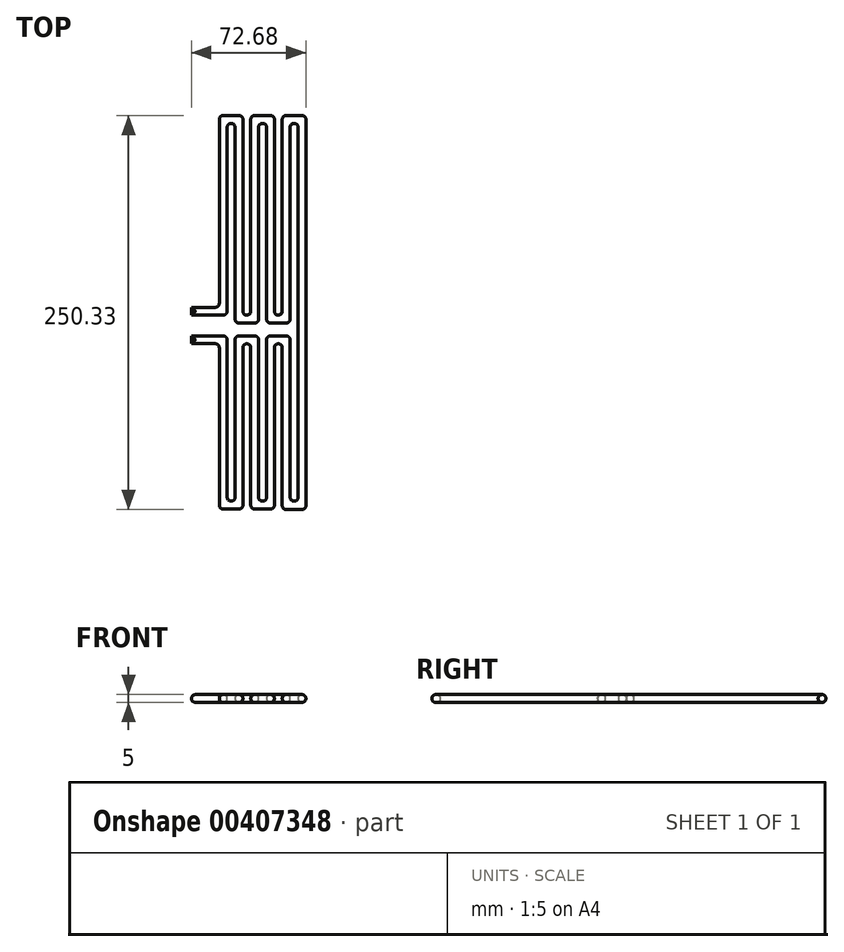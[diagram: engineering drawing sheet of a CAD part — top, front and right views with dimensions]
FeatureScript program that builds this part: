
annotation { "Feature Type Name" : "Feature", "Feature Type Description" : "" }
export const myFeature = defineFeature(function(context is Context, id is Id, definition is map)
    precondition{}
    {
        {
            var Q0;
            Q0=qCreatedBy(makeId("Top.planeOp"),FACE);
            var sketch = newSketch(context, id + "F0", { "sketchPlane" : qUnion([Q0])});
            skLineSegment(sketch, "E0.bottom", {"start": v(0, 0) * mm, "end": v(17.68, 0) * mm});
            skLineSegment(sketch, "E0.top", {"start": v(0, 5) * mm, "end": v(15.18, 5) * mm});
            skLineSegment(sketch, "E0.left", {"start": v(0, 0) * mm, "end": v(0, 5) * mm});
            skLineSegment(sketch, "E1.bottom", {"start": v(17.68, 0) * mm, "end": v(20.18, 0) * mm});
            skLineSegment(sketch, "E1.left", {"start": v(17.68, 7.5) * mm, "end": v(17.68, 121.85) * mm});
            skLineSegment(sketch, "E1.right", {"start": v(22.68, 2.5) * mm, "end": v(22.68, 119.35) * mm});
            skLineSegment(sketch, "E2.bottom", {"start": v(25.18, 121.85) * mm, "end": v(25.18, 121.85) * mm});
            skLineSegment(sketch, "E2.top", {"start": v(20.18, 126.85) * mm, "end": v(30.18, 126.85) * mm});
            skLineSegment(sketch, "E2.left", {"start": v(17.68, 121.85) * mm, "end": v(17.68, 124.35) * mm});
            skLineSegment(sketch, "E2.right", {"start": v(32.68, 121.85) * mm, "end": v(32.68, 124.35) * mm});
            skLineSegment(sketch, "E3.left", {"start": v(32.68, 121.85) * mm, "end": v(32.68, 2.5) * mm});
            skLineSegment(sketch, "E3.right", {"start": v(27.68, 119.35) * mm, "end": v(27.68, 0) * mm});
            skLineSegment(sketch, "E4.bottom", {"start": v(35.18, 0) * mm, "end": v(35.18, 0) * mm});
            skLineSegment(sketch, "E4.top", {"start": v(30.18, -5) * mm, "end": v(40.18, -5) * mm});
            skLineSegment(sketch, "E4.left", {"start": v(27.68, 0) * mm, "end": v(27.68, -2.5) * mm});
            skLineSegment(sketch, "E4.right", {"start": v(42.68, 0) * mm, "end": v(42.68, -2.5) * mm});
            skLineSegment(sketch, "E5.left", {"start": v(42.68, 0) * mm, "end": v(42.68, 119.35) * mm});
            skLineSegment(sketch, "E5.right", {"start": v(37.68, 2.5) * mm, "end": v(37.68, 121.85) * mm});
            skLineSegment(sketch, "E6.bottom", {"start": v(45.18, 121.85) * mm, "end": v(45.18, 121.85) * mm});
            skLineSegment(sketch, "E6.top", {"start": v(40.18, 126.85) * mm, "end": v(50.18, 126.85) * mm});
            skLineSegment(sketch, "E6.left", {"start": v(37.68, 121.85) * mm, "end": v(37.68, 124.35) * mm});
            skLineSegment(sketch, "E6.right", {"start": v(52.68, 121.85) * mm, "end": v(52.68, 124.35) * mm});
            skLineSegment(sketch, "E7.left", {"start": v(52.68, 121.85) * mm, "end": v(52.68, 2.5) * mm});
            skLineSegment(sketch, "E7.right", {"start": v(47.68, 119.35) * mm, "end": v(47.68, 0) * mm});
            skLineSegment(sketch, "E8.bottom", {"start": v(55.18, 0) * mm, "end": v(55.18, 0) * mm});
            skLineSegment(sketch, "E8.top", {"start": v(50.18, -5) * mm, "end": v(60.18, -5) * mm});
            skLineSegment(sketch, "E8.left", {"start": v(47.68, 0) * mm, "end": v(47.68, -2.5) * mm});
            skLineSegment(sketch, "E8.right", {"start": v(62.68, 0) * mm, "end": v(62.68, -2.5) * mm});
            skLineSegment(sketch, "E9.left", {"start": v(62.68, 0) * mm, "end": v(62.68, 119.35) * mm});
            skLineSegment(sketch, "E9.right", {"start": v(57.68, 2.5) * mm, "end": v(57.68, 121.85) * mm});
            skLineSegment(sketch, "E10.bottom", {"start": v(65.18, 121.85) * mm, "end": v(65.18, 121.85) * mm});
            skLineSegment(sketch, "E10.top", {"start": v(60.18, 126.85) * mm, "end": v(70.18, 126.85) * mm});
            skLineSegment(sketch, "E10.left", {"start": v(57.68, 121.85) * mm, "end": v(57.68, 124.35) * mm});
            skLineSegment(sketch, "E10.right", {"start": v(72.68, 121.85) * mm, "end": v(72.68, 124.35) * mm});
            skLineSegment(sketch, "E11.left", {"start": v(72.68, 121.85) * mm, "end": v(72.68, -118.15) * mm});
            skLineSegment(sketch, "E11.right", {"start": v(67.68, 119.35) * mm, "end": v(67.68, -115.65) * mm});
            skLineSegment(sketch, "E12.bottom", {"start": v(65.18, -118.15) * mm, "end": v(65.18, -118.15) * mm});
            skLineSegment(sketch, "E12.top", {"start": v(70.18, -123.48) * mm, "end": v(60.18, -123.48) * mm});
            skLineSegment(sketch, "E12.left", {"start": v(72.68, -118.15) * mm, "end": v(72.68, -120.98) * mm});
            skLineSegment(sketch, "E12.right", {"start": v(57.68, -118.15) * mm, "end": v(57.68, -120.98) * mm});
            skLineSegment(sketch, "E13.left", {"start": v(57.68, -118.15) * mm, "end": v(57.68, -20.65) * mm});
            skLineSegment(sketch, "E13.right", {"start": v(62.68, -115.65) * mm, "end": v(62.68, -18.15) * mm});
            skLineSegment(sketch, "E14.bottom", {"start": v(55.18, -18.15) * mm, "end": v(55.18, -18.15) * mm});
            skLineSegment(sketch, "E14.top", {"start": v(60.18, -13.15) * mm, "end": v(50.18, -13.15) * mm});
            skLineSegment(sketch, "E14.left", {"start": v(62.68, -18.15) * mm, "end": v(62.68, -15.65) * mm});
            skLineSegment(sketch, "E14.right", {"start": v(47.68, -18.15) * mm, "end": v(47.68, -15.65) * mm});
            skLineSegment(sketch, "E15.left", {"start": v(47.68, -18.15) * mm, "end": v(47.68, -115.65) * mm});
            skLineSegment(sketch, "E15.right", {"start": v(52.68, -20.65) * mm, "end": v(52.68, -118.15) * mm});
            skLineSegment(sketch, "E16.bottom", {"start": v(45.18, -118.15) * mm, "end": v(45.18, -118.15) * mm});
            skLineSegment(sketch, "E16.top", {"start": v(50.18, -123.15) * mm, "end": v(40.18, -123.15) * mm});
            skLineSegment(sketch, "E16.left", {"start": v(52.68, -118.15) * mm, "end": v(52.68, -120.65) * mm});
            skLineSegment(sketch, "E16.right", {"start": v(37.68, -118.15) * mm, "end": v(37.68, -120.65) * mm});
            skLineSegment(sketch, "E17.left", {"start": v(37.68, -118.15) * mm, "end": v(37.68, -20.65) * mm});
            skLineSegment(sketch, "E17.right", {"start": v(42.68, -115.65) * mm, "end": v(42.68, -18.15) * mm});
            skLineSegment(sketch, "E18.bottom", {"start": v(35.18, -18.15) * mm, "end": v(35.18, -18.15) * mm});
            skLineSegment(sketch, "E18.top", {"start": v(40.18, -13.15) * mm, "end": v(30.18, -13.15) * mm});
            skLineSegment(sketch, "E18.left", {"start": v(42.68, -18.15) * mm, "end": v(42.68, -15.65) * mm});
            skLineSegment(sketch, "E18.right", {"start": v(27.68, -18.15) * mm, "end": v(27.68, -15.65) * mm});
            skLineSegment(sketch, "E19.left", {"start": v(27.68, -18.15) * mm, "end": v(27.68, -115.65) * mm});
            skLineSegment(sketch, "E19.right", {"start": v(32.68, -20.65) * mm, "end": v(32.68, -118.15) * mm});
            skLineSegment(sketch, "E20.bottom", {"start": v(25.18, -118.15) * mm, "end": v(25.18, -118.15) * mm});
            skLineSegment(sketch, "E20.top", {"start": v(30.18, -123.15) * mm, "end": v(20.18, -123.15) * mm});
            skLineSegment(sketch, "E20.left", {"start": v(32.68, -118.15) * mm, "end": v(32.68, -120.65) * mm});
            skLineSegment(sketch, "E20.right", {"start": v(17.68, -118.15) * mm, "end": v(17.68, -120.65) * mm});
            skLineSegment(sketch, "E21.left", {"start": v(17.68, -118.15) * mm, "end": v(17.68, -20.65) * mm});
            skLineSegment(sketch, "E21.right", {"start": v(22.68, -115.65) * mm, "end": v(22.68, -18.15) * mm});
            skLineSegment(sketch, "E22.bottom", {"start": v(15.18, -18.15) * mm, "end": v(0, -18.15) * mm});
            skLineSegment(sketch, "E22.top", {"start": v(20.18, -13.15) * mm, "end": v(0, -13.15) * mm});
            skLineSegment(sketch, "E22.left", {"start": v(22.68, -18.15) * mm, "end": v(22.68, -15.65) * mm});
            skLineSegment(sketch, "E22.right", {"start": v(0, -18.15) * mm, "end": v(0, -13.15) * mm});
            skPoint(sketch, "E23.visualSharp", {"position": v(17.68, 5) * mm});
            skArc(sketch, "E23.filletArc", {"start": v(15.18, 5) * mm, "mid": v(16.95, 5.73) * mm, "end": v(17.68, 7.5) * mm});
            skPoint(sketch, "E24.visualSharp", {"position": v(22.68, 0) * mm});
            skArc(sketch, "E24.filletArc", {"start": v(20.18, 0) * mm, "mid": v(21.95, 0.73) * mm, "end": v(22.68, 2.5) * mm});
            skPoint(sketch, "E25.visualSharp", {"position": v(27.68, -5) * mm});
            skArc(sketch, "E25.filletArc", {"start": v(27.68, -2.5) * mm, "mid": v(28.41, -4.27) * mm, "end": v(30.18, -5) * mm});
            skPoint(sketch, "E26.visualSharp", {"position": v(32.68, 0) * mm});
            skArc(sketch, "E26.filletArc", {"start": v(32.68, 2.5) * mm, "mid": v(33.41, 0.73) * mm, "end": v(35.18, 0) * mm});
            skPoint(sketch, "E27.visualSharp", {"position": v(37.68, 0) * mm});
            skArc(sketch, "E27.filletArc", {"start": v(35.18, 0) * mm, "mid": v(36.95, 0.73) * mm, "end": v(37.68, 2.5) * mm});
            skPoint(sketch, "E28.visualSharp", {"position": v(42.68, -5) * mm});
            skArc(sketch, "E28.filletArc", {"start": v(40.18, -5) * mm, "mid": v(41.95, -4.27) * mm, "end": v(42.68, -2.5) * mm});
            skPoint(sketch, "E29.visualSharp", {"position": v(47.68, -5) * mm});
            skArc(sketch, "E29.filletArc", {"start": v(47.68, -2.5) * mm, "mid": v(48.41, -4.27) * mm, "end": v(50.18, -5) * mm});
            skPoint(sketch, "E30.visualSharp", {"position": v(52.68, 0) * mm});
            skArc(sketch, "E30.filletArc", {"start": v(52.68, 2.5) * mm, "mid": v(53.41, 0.73) * mm, "end": v(55.18, 0) * mm});
            skPoint(sketch, "E31.visualSharp", {"position": v(57.68, 0) * mm});
            skArc(sketch, "E31.filletArc", {"start": v(55.18, 0) * mm, "mid": v(56.95, 0.73) * mm, "end": v(57.68, 2.5) * mm});
            skPoint(sketch, "E32.visualSharp", {"position": v(62.68, -5) * mm});
            skArc(sketch, "E32.filletArc", {"start": v(60.18, -5) * mm, "mid": v(61.95, -4.27) * mm, "end": v(62.68, -2.5) * mm});
            skPoint(sketch, "E33.visualSharp", {"position": v(17.68, 126.85) * mm});
            skArc(sketch, "E33.filletArc", {"start": v(20.18, 126.85) * mm, "mid": v(18.41, 126.12) * mm, "end": v(17.68, 124.35) * mm});
            skPoint(sketch, "E34.visualSharp", {"position": v(22.68, 121.85) * mm});
            skArc(sketch, "E34.filletArc", {"start": v(25.18, 121.85) * mm, "mid": v(23.41, 121.12) * mm, "end": v(22.68, 119.35) * mm});
            skPoint(sketch, "E35.visualSharp", {"position": v(27.68, 121.85) * mm});
            skArc(sketch, "E35.filletArc", {"start": v(27.68, 119.35) * mm, "mid": v(26.95, 121.12) * mm, "end": v(25.18, 121.85) * mm});
            skPoint(sketch, "E36.visualSharp", {"position": v(32.68, 126.85) * mm});
            skArc(sketch, "E36.filletArc", {"start": v(32.68, 124.35) * mm, "mid": v(31.95, 126.12) * mm, "end": v(30.18, 126.85) * mm});
            skPoint(sketch, "E37.visualSharp", {"position": v(37.68, 126.85) * mm});
            skArc(sketch, "E37.filletArc", {"start": v(40.18, 126.85) * mm, "mid": v(38.41, 126.12) * mm, "end": v(37.68, 124.35) * mm});
            skPoint(sketch, "E38.visualSharp", {"position": v(52.68, 126.85) * mm});
            skArc(sketch, "E38.filletArc", {"start": v(52.68, 124.35) * mm, "mid": v(51.95, 126.12) * mm, "end": v(50.18, 126.85) * mm});
            skPoint(sketch, "E39.visualSharp", {"position": v(42.68, 121.85) * mm});
            skArc(sketch, "E39.filletArc", {"start": v(45.18, 121.85) * mm, "mid": v(43.41, 121.12) * mm, "end": v(42.68, 119.35) * mm});
            skPoint(sketch, "E40.visualSharp", {"position": v(47.68, 121.85) * mm});
            skArc(sketch, "E40.filletArc", {"start": v(47.68, 119.35) * mm, "mid": v(46.95, 121.12) * mm, "end": v(45.18, 121.85) * mm});
            skPoint(sketch, "E41.visualSharp", {"position": v(57.68, 126.85) * mm});
            skArc(sketch, "E41.filletArc", {"start": v(60.18, 126.85) * mm, "mid": v(58.41, 126.12) * mm, "end": v(57.68, 124.35) * mm});
            skPoint(sketch, "E42.visualSharp", {"position": v(72.68, 126.85) * mm});
            skArc(sketch, "E42.filletArc", {"start": v(72.68, 124.35) * mm, "mid": v(71.95, 126.12) * mm, "end": v(70.18, 126.85) * mm});
            skPoint(sketch, "E43.visualSharp", {"position": v(62.68, 121.85) * mm});
            skArc(sketch, "E43.filletArc", {"start": v(65.18, 121.85) * mm, "mid": v(63.41, 121.12) * mm, "end": v(62.68, 119.35) * mm});
            skPoint(sketch, "E44.visualSharp", {"position": v(67.68, 121.85) * mm});
            skArc(sketch, "E44.filletArc", {"start": v(67.68, 119.35) * mm, "mid": v(66.95, 121.12) * mm, "end": v(65.18, 121.85) * mm});
            skPoint(sketch, "E45.visualSharp", {"position": v(72.68, -123.48) * mm});
            skArc(sketch, "E45.filletArc", {"start": v(70.18, -123.48) * mm, "mid": v(71.95, -122.75) * mm, "end": v(72.68, -120.98) * mm});
            skPoint(sketch, "E46.visualSharp", {"position": v(67.68, -118.15) * mm});
            skArc(sketch, "E46.filletArc", {"start": v(65.18, -118.15) * mm, "mid": v(66.95, -117.42) * mm, "end": v(67.68, -115.65) * mm});
            skPoint(sketch, "E47.visualSharp", {"position": v(62.68, -118.15) * mm});
            skArc(sketch, "E47.filletArc", {"start": v(62.68, -115.65) * mm, "mid": v(63.41, -117.42) * mm, "end": v(65.18, -118.15) * mm});
            skPoint(sketch, "E48.visualSharp", {"position": v(57.68, -123.48) * mm});
            skArc(sketch, "E48.filletArc", {"start": v(57.68, -120.98) * mm, "mid": v(58.41, -122.75) * mm, "end": v(60.18, -123.48) * mm});
            skPoint(sketch, "E49.visualSharp", {"position": v(52.68, -123.15) * mm});
            skArc(sketch, "E49.filletArc", {"start": v(50.18, -123.15) * mm, "mid": v(51.95, -122.42) * mm, "end": v(52.68, -120.65) * mm});
            skPoint(sketch, "E50.visualSharp", {"position": v(47.68, -118.15) * mm});
            skArc(sketch, "E50.filletArc", {"start": v(45.18, -118.15) * mm, "mid": v(46.95, -117.42) * mm, "end": v(47.68, -115.65) * mm});
            skPoint(sketch, "E51.visualSharp", {"position": v(42.68, -118.15) * mm});
            skArc(sketch, "E51.filletArc", {"start": v(42.68, -115.65) * mm, "mid": v(43.41, -117.42) * mm, "end": v(45.18, -118.15) * mm});
            skPoint(sketch, "E52.visualSharp", {"position": v(37.68, -123.15) * mm});
            skArc(sketch, "E52.filletArc", {"start": v(37.68, -120.65) * mm, "mid": v(38.41, -122.42) * mm, "end": v(40.18, -123.15) * mm});
            skPoint(sketch, "E53.visualSharp", {"position": v(32.68, -123.15) * mm});
            skArc(sketch, "E53.filletArc", {"start": v(30.18, -123.15) * mm, "mid": v(31.95, -122.42) * mm, "end": v(32.68, -120.65) * mm});
            skPoint(sketch, "E54.visualSharp", {"position": v(27.68, -118.15) * mm});
            skArc(sketch, "E54.filletArc", {"start": v(25.18, -118.15) * mm, "mid": v(26.95, -117.42) * mm, "end": v(27.68, -115.65) * mm});
            skPoint(sketch, "E55.visualSharp", {"position": v(22.68, -118.15) * mm});
            skArc(sketch, "E55.filletArc", {"start": v(22.68, -115.65) * mm, "mid": v(23.41, -117.42) * mm, "end": v(25.18, -118.15) * mm});
            skPoint(sketch, "E56.visualSharp", {"position": v(17.68, -123.15) * mm});
            skArc(sketch, "E56.filletArc", {"start": v(17.68, -120.65) * mm, "mid": v(18.41, -122.42) * mm, "end": v(20.18, -123.15) * mm});
            skPoint(sketch, "E57.visualSharp", {"position": v(22.68, -13.15) * mm});
            skArc(sketch, "E57.filletArc", {"start": v(22.68, -15.65) * mm, "mid": v(21.95, -13.88) * mm, "end": v(20.18, -13.15) * mm});
            skPoint(sketch, "E58.visualSharp", {"position": v(17.68, -18.15) * mm});
            skArc(sketch, "E58.filletArc", {"start": v(17.68, -20.65) * mm, "mid": v(16.95, -18.88) * mm, "end": v(15.18, -18.15) * mm});
            skPoint(sketch, "E59.visualSharp", {"position": v(27.68, -13.15) * mm});
            skArc(sketch, "E59.filletArc", {"start": v(30.18, -13.15) * mm, "mid": v(28.41, -13.88) * mm, "end": v(27.68, -15.65) * mm});
            skPoint(sketch, "E60.visualSharp", {"position": v(42.68, -13.15) * mm});
            skArc(sketch, "E60.filletArc", {"start": v(42.68, -15.65) * mm, "mid": v(41.95, -13.88) * mm, "end": v(40.18, -13.15) * mm});
            skPoint(sketch, "E61.visualSharp", {"position": v(62.68, -13.15) * mm});
            skArc(sketch, "E61.filletArc", {"start": v(62.68, -15.65) * mm, "mid": v(61.95, -13.88) * mm, "end": v(60.18, -13.15) * mm});
            skPoint(sketch, "E62.visualSharp", {"position": v(47.68, -13.15) * mm});
            skArc(sketch, "E62.filletArc", {"start": v(50.18, -13.15) * mm, "mid": v(48.41, -13.88) * mm, "end": v(47.68, -15.65) * mm});
            skPoint(sketch, "E63.visualSharp", {"position": v(52.68, -18.15) * mm});
            skArc(sketch, "E63.filletArc", {"start": v(55.18, -18.15) * mm, "mid": v(53.41, -18.88) * mm, "end": v(52.68, -20.65) * mm});
            skPoint(sketch, "E64.visualSharp", {"position": v(57.68, -18.15) * mm});
            skArc(sketch, "E64.filletArc", {"start": v(57.68, -20.65) * mm, "mid": v(56.95, -18.88) * mm, "end": v(55.18, -18.15) * mm});
            skPoint(sketch, "E65.visualSharp", {"position": v(37.68, -18.15) * mm});
            skArc(sketch, "E65.filletArc", {"start": v(37.68, -20.65) * mm, "mid": v(36.95, -18.88) * mm, "end": v(35.18, -18.15) * mm});
            skPoint(sketch, "E66.visualSharp", {"position": v(32.68, -18.15) * mm});
            skArc(sketch, "E66.filletArc", {"start": v(35.18, -18.15) * mm, "mid": v(33.41, -18.88) * mm, "end": v(32.68, -20.65) * mm});
            skSolve(sketch);
        }
        {
            var Q0;
            Q0=makeQuery(id+"F0.imprint","IMPRINT",FACE,{"disambiguationData":[TD([[makeQuery(id+"F0.imprint","IMPRINT",EDGE,{"derivedFrom":sQuery(id+"F0.wireOp",EDGE,"E0.bottom")}),1.0]])]});
            extrude(context, id + "F1", {"entities" : qUnion([Q0]), "depth" : 5 * mm});
        }
        {
            var Q0;
            Q0=makeQuery(id+"F1.opExtrude","CAP_FACE",FACE,{"disambiguationData":[OSD([sQuery(id+"F0.wireOp",EDGE,"E0.bottom"),sQuery(id+"F0.wireOp",EDGE,"E0.top"),sQuery(id+"F0.wireOp",EDGE,"E0.left"),sQuery(id+"F0.wireOp",EDGE,"E1.bottom"),sQuery(id+"F0.wireOp",EDGE,"E1.left"),sQuery(id+"F0.wireOp",EDGE,"E1.right"),sQuery(id+"F0.wireOp",EDGE,"E2.top"),sQuery(id+"F0.wireOp",EDGE,"E2.left"),sQuery(id+"F0.wireOp",EDGE,"E2.right"),sQuery(id+"F0.wireOp",EDGE,"E3.left"),sQuery(id+"F0.wireOp",EDGE,"E3.right"),sQuery(id+"F0.wireOp",EDGE,"E4.top"),sQuery(id+"F0.wireOp",EDGE,"E4.left"),sQuery(id+"F0.wireOp",EDGE,"E4.right"),sQuery(id+"F0.wireOp",EDGE,"E5.left"),sQuery(id+"F0.wireOp",EDGE,"E5.right"),sQuery(id+"F0.wireOp",EDGE,"E6.top"),sQuery(id+"F0.wireOp",EDGE,"E6.left"),sQuery(id+"F0.wireOp",EDGE,"E6.right"),sQuery(id+"F0.wireOp",EDGE,"E7.left"),sQuery(id+"F0.wireOp",EDGE,"E7.right"),sQuery(id+"F0.wireOp",EDGE,"E8.top"),sQuery(id+"F0.wireOp",EDGE,"E8.left"),sQuery(id+"F0.wireOp",EDGE,"E8.right"),sQuery(id+"F0.wireOp",EDGE,"E9.left"),sQuery(id+"F0.wireOp",EDGE,"E9.right"),sQuery(id+"F0.wireOp",EDGE,"E10.top"),sQuery(id+"F0.wireOp",EDGE,"E10.left"),sQuery(id+"F0.wireOp",EDGE,"E10.right"),sQuery(id+"F0.wireOp",EDGE,"E11.left"),sQuery(id+"F0.wireOp",EDGE,"E11.right"),sQuery(id+"F0.wireOp",EDGE,"E12.top"),sQuery(id+"F0.wireOp",EDGE,"E12.left"),sQuery(id+"F0.wireOp",EDGE,"E12.right"),sQuery(id+"F0.wireOp",EDGE,"E13.left"),sQuery(id+"F0.wireOp",EDGE,"E13.right"),sQuery(id+"F0.wireOp",EDGE,"E14.top"),sQuery(id+"F0.wireOp",EDGE,"E14.left"),sQuery(id+"F0.wireOp",EDGE,"E14.right"),sQuery(id+"F0.wireOp",EDGE,"E15.left"),sQuery(id+"F0.wireOp",EDGE,"E15.right"),sQuery(id+"F0.wireOp",EDGE,"E16.top"),sQuery(id+"F0.wireOp",EDGE,"E16.left"),sQuery(id+"F0.wireOp",EDGE,"E16.right"),sQuery(id+"F0.wireOp",EDGE,"E17.left"),sQuery(id+"F0.wireOp",EDGE,"E17.right"),sQuery(id+"F0.wireOp",EDGE,"E18.top"),sQuery(id+"F0.wireOp",EDGE,"E18.left"),sQuery(id+"F0.wireOp",EDGE,"E18.right"),sQuery(id+"F0.wireOp",EDGE,"E19.left"),sQuery(id+"F0.wireOp",EDGE,"E19.right"),sQuery(id+"F0.wireOp",EDGE,"E20.top"),sQuery(id+"F0.wireOp",EDGE,"E20.left"),sQuery(id+"F0.wireOp",EDGE,"E20.right"),sQuery(id+"F0.wireOp",EDGE,"E21.left"),sQuery(id+"F0.wireOp",EDGE,"E21.right"),sQuery(id+"F0.wireOp",EDGE,"E22.bottom"),sQuery(id+"F0.wireOp",EDGE,"E22.top"),sQuery(id+"F0.wireOp",EDGE,"E22.left"),sQuery(id+"F0.wireOp",EDGE,"E22.right"),sQuery(id+"F0.wireOp",EDGE,"E23.filletArc"),sQuery(id+"F0.wireOp",EDGE,"E24.filletArc"),sQuery(id+"F0.wireOp",EDGE,"E25.filletArc"),sQuery(id+"F0.wireOp",EDGE,"E26.filletArc"),sQuery(id+"F0.wireOp",EDGE,"E27.filletArc"),sQuery(id+"F0.wireOp",EDGE,"E28.filletArc"),sQuery(id+"F0.wireOp",EDGE,"E29.filletArc"),sQuery(id+"F0.wireOp",EDGE,"E30.filletArc"),sQuery(id+"F0.wireOp",EDGE,"E31.filletArc"),sQuery(id+"F0.wireOp",EDGE,"E32.filletArc"),sQuery(id+"F0.wireOp",EDGE,"E33.filletArc"),sQuery(id+"F0.wireOp",EDGE,"E34.filletArc"),sQuery(id+"F0.wireOp",EDGE,"E35.filletArc"),sQuery(id+"F0.wireOp",EDGE,"E36.filletArc"),sQuery(id+"F0.wireOp",EDGE,"E37.filletArc"),sQuery(id+"F0.wireOp",EDGE,"E38.filletArc"),sQuery(id+"F0.wireOp",EDGE,"E39.filletArc"),sQuery(id+"F0.wireOp",EDGE,"E40.filletArc"),sQuery(id+"F0.wireOp",EDGE,"E41.filletArc"),sQuery(id+"F0.wireOp",EDGE,"E42.filletArc"),sQuery(id+"F0.wireOp",EDGE,"E43.filletArc"),sQuery(id+"F0.wireOp",EDGE,"E44.filletArc"),sQuery(id+"F0.wireOp",EDGE,"E45.filletArc"),sQuery(id+"F0.wireOp",EDGE,"E46.filletArc"),sQuery(id+"F0.wireOp",EDGE,"E47.filletArc"),sQuery(id+"F0.wireOp",EDGE,"E48.filletArc"),sQuery(id+"F0.wireOp",EDGE,"E49.filletArc"),sQuery(id+"F0.wireOp",EDGE,"E50.filletArc"),sQuery(id+"F0.wireOp",EDGE,"E51.filletArc"),sQuery(id+"F0.wireOp",EDGE,"E52.filletArc"),sQuery(id+"F0.wireOp",EDGE,"E53.filletArc"),sQuery(id+"F0.wireOp",EDGE,"E54.filletArc"),sQuery(id+"F0.wireOp",EDGE,"E55.filletArc"),sQuery(id+"F0.wireOp",EDGE,"E56.filletArc"),sQuery(id+"F0.wireOp",EDGE,"E57.filletArc"),sQuery(id+"F0.wireOp",EDGE,"E58.filletArc"),sQuery(id+"F0.wireOp",EDGE,"E59.filletArc"),sQuery(id+"F0.wireOp",EDGE,"E60.filletArc"),sQuery(id+"F0.wireOp",EDGE,"E61.filletArc"),sQuery(id+"F0.wireOp",EDGE,"E62.filletArc"),sQuery(id+"F0.wireOp",EDGE,"E63.filletArc"),sQuery(id+"F0.wireOp",EDGE,"E64.filletArc"),sQuery(id+"F0.wireOp",EDGE,"E65.filletArc"),sQuery(id+"F0.wireOp",EDGE,"E66.filletArc")])],"isStart":false});
            var Q1;
            Q1=makeQuery(id+"F1.opExtrude","CAP_FACE",FACE,{"disambiguationData":[OSD([sQuery(id+"F0.wireOp",EDGE,"E0.bottom"),sQuery(id+"F0.wireOp",EDGE,"E0.top"),sQuery(id+"F0.wireOp",EDGE,"E0.left"),sQuery(id+"F0.wireOp",EDGE,"E1.bottom"),sQuery(id+"F0.wireOp",EDGE,"E1.left"),sQuery(id+"F0.wireOp",EDGE,"E1.right"),sQuery(id+"F0.wireOp",EDGE,"E2.top"),sQuery(id+"F0.wireOp",EDGE,"E2.left"),sQuery(id+"F0.wireOp",EDGE,"E2.right"),sQuery(id+"F0.wireOp",EDGE,"E3.left"),sQuery(id+"F0.wireOp",EDGE,"E3.right"),sQuery(id+"F0.wireOp",EDGE,"E4.top"),sQuery(id+"F0.wireOp",EDGE,"E4.left"),sQuery(id+"F0.wireOp",EDGE,"E4.right"),sQuery(id+"F0.wireOp",EDGE,"E5.left"),sQuery(id+"F0.wireOp",EDGE,"E5.right"),sQuery(id+"F0.wireOp",EDGE,"E6.top"),sQuery(id+"F0.wireOp",EDGE,"E6.left"),sQuery(id+"F0.wireOp",EDGE,"E6.right"),sQuery(id+"F0.wireOp",EDGE,"E7.left"),sQuery(id+"F0.wireOp",EDGE,"E7.right"),sQuery(id+"F0.wireOp",EDGE,"E8.top"),sQuery(id+"F0.wireOp",EDGE,"E8.left"),sQuery(id+"F0.wireOp",EDGE,"E8.right"),sQuery(id+"F0.wireOp",EDGE,"E9.left"),sQuery(id+"F0.wireOp",EDGE,"E9.right"),sQuery(id+"F0.wireOp",EDGE,"E10.top"),sQuery(id+"F0.wireOp",EDGE,"E10.left"),sQuery(id+"F0.wireOp",EDGE,"E10.right"),sQuery(id+"F0.wireOp",EDGE,"E11.left"),sQuery(id+"F0.wireOp",EDGE,"E11.right"),sQuery(id+"F0.wireOp",EDGE,"E12.top"),sQuery(id+"F0.wireOp",EDGE,"E12.left"),sQuery(id+"F0.wireOp",EDGE,"E12.right"),sQuery(id+"F0.wireOp",EDGE,"E13.left"),sQuery(id+"F0.wireOp",EDGE,"E13.right"),sQuery(id+"F0.wireOp",EDGE,"E14.top"),sQuery(id+"F0.wireOp",EDGE,"E14.left"),sQuery(id+"F0.wireOp",EDGE,"E14.right"),sQuery(id+"F0.wireOp",EDGE,"E15.left"),sQuery(id+"F0.wireOp",EDGE,"E15.right"),sQuery(id+"F0.wireOp",EDGE,"E16.top"),sQuery(id+"F0.wireOp",EDGE,"E16.left"),sQuery(id+"F0.wireOp",EDGE,"E16.right"),sQuery(id+"F0.wireOp",EDGE,"E17.left"),sQuery(id+"F0.wireOp",EDGE,"E17.right"),sQuery(id+"F0.wireOp",EDGE,"E18.top"),sQuery(id+"F0.wireOp",EDGE,"E18.left"),sQuery(id+"F0.wireOp",EDGE,"E18.right"),sQuery(id+"F0.wireOp",EDGE,"E19.left"),sQuery(id+"F0.wireOp",EDGE,"E19.right"),sQuery(id+"F0.wireOp",EDGE,"E20.top"),sQuery(id+"F0.wireOp",EDGE,"E20.left"),sQuery(id+"F0.wireOp",EDGE,"E20.right"),sQuery(id+"F0.wireOp",EDGE,"E21.left"),sQuery(id+"F0.wireOp",EDGE,"E21.right"),sQuery(id+"F0.wireOp",EDGE,"E22.bottom"),sQuery(id+"F0.wireOp",EDGE,"E22.top"),sQuery(id+"F0.wireOp",EDGE,"E22.left"),sQuery(id+"F0.wireOp",EDGE,"E22.right"),sQuery(id+"F0.wireOp",EDGE,"E23.filletArc"),sQuery(id+"F0.wireOp",EDGE,"E24.filletArc"),sQuery(id+"F0.wireOp",EDGE,"E25.filletArc"),sQuery(id+"F0.wireOp",EDGE,"E26.filletArc"),sQuery(id+"F0.wireOp",EDGE,"E27.filletArc"),sQuery(id+"F0.wireOp",EDGE,"E28.filletArc"),sQuery(id+"F0.wireOp",EDGE,"E29.filletArc"),sQuery(id+"F0.wireOp",EDGE,"E30.filletArc"),sQuery(id+"F0.wireOp",EDGE,"E31.filletArc"),sQuery(id+"F0.wireOp",EDGE,"E32.filletArc"),sQuery(id+"F0.wireOp",EDGE,"E33.filletArc"),sQuery(id+"F0.wireOp",EDGE,"E34.filletArc"),sQuery(id+"F0.wireOp",EDGE,"E35.filletArc"),sQuery(id+"F0.wireOp",EDGE,"E36.filletArc"),sQuery(id+"F0.wireOp",EDGE,"E37.filletArc"),sQuery(id+"F0.wireOp",EDGE,"E38.filletArc"),sQuery(id+"F0.wireOp",EDGE,"E39.filletArc"),sQuery(id+"F0.wireOp",EDGE,"E40.filletArc"),sQuery(id+"F0.wireOp",EDGE,"E41.filletArc"),sQuery(id+"F0.wireOp",EDGE,"E42.filletArc"),sQuery(id+"F0.wireOp",EDGE,"E43.filletArc"),sQuery(id+"F0.wireOp",EDGE,"E44.filletArc"),sQuery(id+"F0.wireOp",EDGE,"E45.filletArc"),sQuery(id+"F0.wireOp",EDGE,"E46.filletArc"),sQuery(id+"F0.wireOp",EDGE,"E47.filletArc"),sQuery(id+"F0.wireOp",EDGE,"E48.filletArc"),sQuery(id+"F0.wireOp",EDGE,"E49.filletArc"),sQuery(id+"F0.wireOp",EDGE,"E50.filletArc"),sQuery(id+"F0.wireOp",EDGE,"E51.filletArc"),sQuery(id+"F0.wireOp",EDGE,"E52.filletArc"),sQuery(id+"F0.wireOp",EDGE,"E53.filletArc"),sQuery(id+"F0.wireOp",EDGE,"E54.filletArc"),sQuery(id+"F0.wireOp",EDGE,"E55.filletArc"),sQuery(id+"F0.wireOp",EDGE,"E56.filletArc"),sQuery(id+"F0.wireOp",EDGE,"E57.filletArc"),sQuery(id+"F0.wireOp",EDGE,"E58.filletArc"),sQuery(id+"F0.wireOp",EDGE,"E59.filletArc"),sQuery(id+"F0.wireOp",EDGE,"E60.filletArc"),sQuery(id+"F0.wireOp",EDGE,"E61.filletArc"),sQuery(id+"F0.wireOp",EDGE,"E62.filletArc"),sQuery(id+"F0.wireOp",EDGE,"E63.filletArc"),sQuery(id+"F0.wireOp",EDGE,"E64.filletArc"),sQuery(id+"F0.wireOp",EDGE,"E65.filletArc"),sQuery(id+"F0.wireOp",EDGE,"E66.filletArc")])],"isStart":true});
            fillet(context, id + "F2", {"entities" : qUnion([Q0, Q1]), "radius" : 2.5 * mm, "tangentPropagation" : true, "allowEdgeOverflow" : false});
        }
    });
